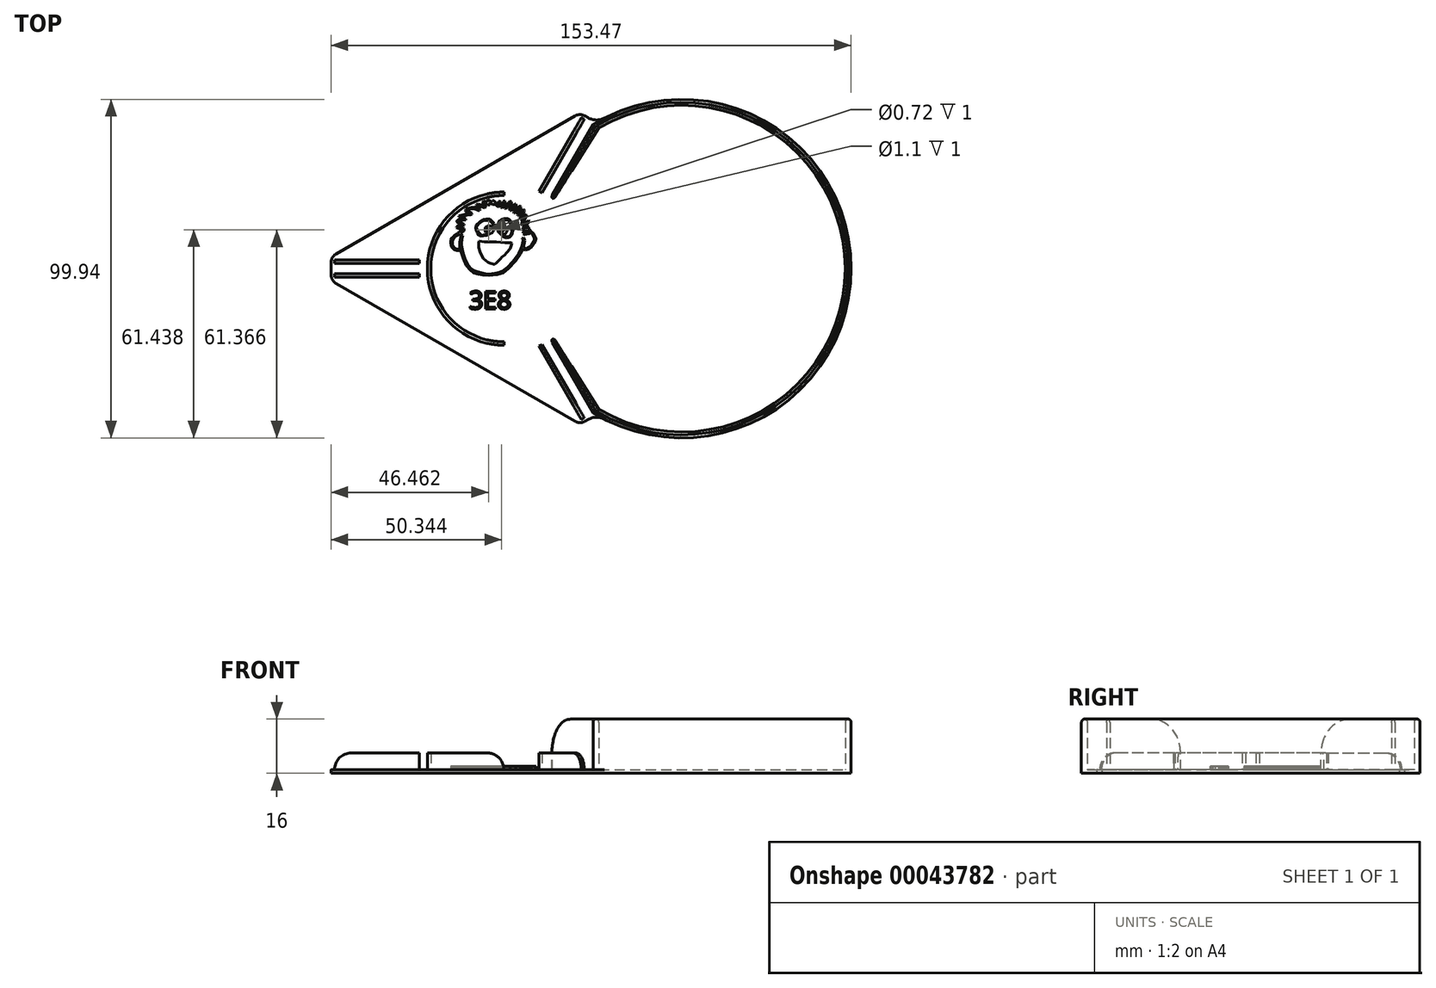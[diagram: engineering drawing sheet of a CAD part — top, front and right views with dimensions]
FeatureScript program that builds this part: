
annotation { "Feature Type Name" : "Feature", "Feature Type Description" : "" }
export const myFeature = defineFeature(function(context is Context, id is Id, definition is map)
    precondition{}
    {
        {
            var Q0;
            Q0=qCreatedBy(makeId("Top.planeOp"),FACE);
            var sketch = newSketch(context, id + "F0", { "sketchPlane" : qUnion([Q0])});
            skCircle(sketch, "E0", {"center": v(0, 0) * mm, "radius": 21.6 * mm, "construction": true});
            skLineSegment(sketch, "E1", {"start": v(0, 0) * mm, "end": v(-25, 0) * mm, "construction": true});
            skLineSegment(sketch, "E2", {"start": v(0, 0) * mm, "end": v(52.5, 0) * mm, "construction": true});
            skCircle(sketch, "E3", {"center": v(52.5, 0) * mm, "radius": 49.97 * mm});
            skLineSegment(sketch, "E4", {"start": v(-25, -1.5) * mm, "end": v(-25, 1.5) * mm, "construction": true});
            skLineSegment(sketch, "E5.bottom", {"start": v(-25, -1.5) * mm, "end": v(-50, -1.5) * mm, "construction": true});
            skLineSegment(sketch, "E5.top", {"start": v(-25, -2.5) * mm, "end": v(-50, -2.5) * mm, "construction": true});
            skLineSegment(sketch, "E5.left", {"start": v(-25, -1.5) * mm, "end": v(-25, -2.5) * mm, "construction": true});
            skLineSegment(sketch, "E5.right", {"start": v(-50, -1.5) * mm, "end": v(-50, -2.5) * mm, "construction": true});
            skLineSegment(sketch, "E6.MirrorCS", {"start": v(-25, 2.5) * mm, "end": v(-50, 2.5) * mm, "construction": true});
            skLineSegment(sketch, "E7.MirrorCS", {"start": v(-25, 1.5) * mm, "end": v(-50, 1.5) * mm, "construction": true});
            skLineSegment(sketch, "E8.MirrorCS", {"start": v(-25, 1.5) * mm, "end": v(-25, 2.5) * mm, "construction": true});
            skLineSegment(sketch, "E9.MirrorCS", {"start": v(-50, 1.5) * mm, "end": v(-50, 2.5) * mm, "construction": true});
            skLineSegment(sketch, "E10.1.0", {"start": v(11.2, -22.4) * mm, "end": v(23.7, -44.05) * mm, "construction": true});
            skLineSegment(sketch, "E10.1.1", {"start": v(14.67, -20.4) * mm, "end": v(27.17, -42.05) * mm, "construction": true});
            skLineSegment(sketch, "E10.1.2", {"start": v(10.33, -22.9) * mm, "end": v(22.83, -44.55) * mm, "construction": true});
            skLineSegment(sketch, "E10.1.3", {"start": v(13.8, -20.9) * mm, "end": v(26.3, -42.55) * mm, "construction": true});
            skLineSegment(sketch, "E10.1.4", {"start": v(13.8, -20.9) * mm, "end": v(14.67, -20.4) * mm, "construction": true});
            skLineSegment(sketch, "E10.1.5", {"start": v(26.3, -42.55) * mm, "end": v(27.17, -42.05) * mm, "construction": true});
            skLineSegment(sketch, "E10.1.6", {"start": v(11.2, -22.4) * mm, "end": v(10.33, -22.9) * mm, "construction": true});
            skLineSegment(sketch, "E10.1.7", {"start": v(23.7, -44.05) * mm, "end": v(22.83, -44.55) * mm, "construction": true});
            skLineSegment(sketch, "E10.2.0", {"start": v(13.8, 20.9) * mm, "end": v(26.3, 42.55) * mm, "construction": true});
            skLineSegment(sketch, "E10.2.1", {"start": v(10.33, 22.9) * mm, "end": v(22.83, 44.55) * mm, "construction": true});
            skLineSegment(sketch, "E10.2.2", {"start": v(14.67, 20.4) * mm, "end": v(27.17, 42.05) * mm, "construction": true});
            skLineSegment(sketch, "E10.2.3", {"start": v(11.2, 22.4) * mm, "end": v(23.7, 44.05) * mm, "construction": true});
            skLineSegment(sketch, "E10.2.4", {"start": v(11.2, 22.4) * mm, "end": v(10.33, 22.9) * mm, "construction": true});
            skLineSegment(sketch, "E10.2.5", {"start": v(23.7, 44.05) * mm, "end": v(22.83, 44.55) * mm, "construction": true});
            skLineSegment(sketch, "E10.2.6", {"start": v(13.8, 20.9) * mm, "end": v(14.67, 20.4) * mm, "construction": true});
            skLineSegment(sketch, "E10.2.7", {"start": v(26.3, 42.55) * mm, "end": v(27.17, 42.05) * mm, "construction": true});
            skCircle(sketch, "E11", {"center": v(0, 0) * mm, "radius": 26 * mm, "construction": true});
            skLineSegment(sketch, "E12.bottom", {"start": v(-51, 3.5) * mm, "end": v(-25.76, 3.5) * mm});
            skLineSegment(sketch, "E12.top", {"start": v(-51, -3.5) * mm, "end": v(-25.76, -3.5) * mm});
            skLineSegment(sketch, "E12.left", {"start": v(-51, 3.5) * mm, "end": v(-51, -3.5) * mm});
            skLineSegment(sketch, "E12.right", {"start": v(-25.76, 3.5) * mm, "end": v(-25.76, -3.5) * mm, "construction": true});
            skLineSegment(sketch, "E13", {"start": v(-50, -2.5) * mm, "end": v(-51, -2.5) * mm, "construction": true});
            skLineSegment(sketch, "E14", {"start": v(-50, 2.5) * mm, "end": v(-50, 3.5) * mm, "construction": true});
            skLineSegment(sketch, "E15", {"start": v(-25, 0) * mm, "end": v(-51, 0) * mm, "construction": true});
            skLineSegment(sketch, "E16.1.0", {"start": v(22.47, -45.92) * mm, "end": v(9.85, -24.06) * mm});
            skLineSegment(sketch, "E16.1.1", {"start": v(22.47, -45.92) * mm, "end": v(28.53, -42.42) * mm});
            skLineSegment(sketch, "E16.1.2", {"start": v(28.53, -42.42) * mm, "end": v(15.91, -20.56) * mm});
            skLineSegment(sketch, "E16.2.0", {"start": v(28.53, 42.42) * mm, "end": v(15.91, 20.56) * mm});
            skLineSegment(sketch, "E16.2.1", {"start": v(28.53, 42.42) * mm, "end": v(22.47, 45.92) * mm});
            skLineSegment(sketch, "E16.2.2", {"start": v(22.47, 45.92) * mm, "end": v(9.85, 24.06) * mm});
            skLineSegment(sketch, "E17", {"start": v(-51, -3.5) * mm, "end": v(22.47, -45.92) * mm});
            skLineSegment(sketch, "E18.MirrorCS", {"start": v(-51, 3.5) * mm, "end": v(22.47, 45.92) * mm});
            skSolve(sketch);
        }
        {
            var Q0;
            Q0 = qSketchRegion(id + "F0", true);
            extrude(context, id + "F1", {"entities" : qUnion([Q0]), "depth" : 1 * mm});
        }
        {
            var Q0;
            Q0=makeQuery(id+"F1.opExtrude","CAP_FACE",FACE,{"disambiguationData":[OSD([sQuery(id+"F0.wireOp",EDGE,"E3"),sQuery(id+"F0.wireOp",EDGE,"E11"),sQuery(id+"F0.wireOp",EDGE,"E12.bottom"),sQuery(id+"F0.wireOp",EDGE,"E12.top"),sQuery(id+"F0.wireOp",EDGE,"E12.left"),sQuery(id+"F0.wireOp",EDGE,"E16.1.0"),sQuery(id+"F0.wireOp",EDGE,"E16.1.1"),sQuery(id+"F0.wireOp",EDGE,"E16.2.1"),sQuery(id+"F0.wireOp",EDGE,"E16.2.2")])],"isStart":false});
            var sketch = newSketch(context, id + "F2", { "sketchPlane" : qUnion([Q0])});
            skLineSegment(sketch, "E19.0", {"start": v(-25, 1.5) * mm, "end": v(-50, 1.5) * mm});
            skLineSegment(sketch, "E20.0", {"start": v(-25, 2.5) * mm, "end": v(-50, 2.5) * mm});
            skLineSegment(sketch, "E21.0", {"start": v(-50, 1.5) * mm, "end": v(-50, 2.5) * mm});
            skLineSegment(sketch, "E22.0", {"start": v(-25, 1.5) * mm, "end": v(-25, 2.5) * mm});
            skLineSegment(sketch, "E23.0", {"start": v(-25, -1.5) * mm, "end": v(-50, -1.5) * mm});
            skLineSegment(sketch, "E24.0", {"start": v(-25, -2.5) * mm, "end": v(-50, -2.5) * mm});
            skLineSegment(sketch, "E25.0", {"start": v(-50, -1.5) * mm, "end": v(-50, -2.5) * mm});
            skLineSegment(sketch, "E26.0", {"start": v(-25, -1.5) * mm, "end": v(-25, -2.5) * mm});
            skLineSegment(sketch, "E27.0", {"start": v(10.33, 22.9) * mm, "end": v(22.83, 44.55) * mm});
            skLineSegment(sketch, "E28.0", {"start": v(11.2, 22.4) * mm, "end": v(23.7, 44.05) * mm});
            skLineSegment(sketch, "E29.0", {"start": v(23.7, 44.05) * mm, "end": v(22.83, 44.55) * mm});
            skLineSegment(sketch, "E30.0", {"start": v(11.2, 22.4) * mm, "end": v(10.33, 22.9) * mm});
            skLineSegment(sketch, "E31.0", {"start": v(11.2, -22.4) * mm, "end": v(23.7, -44.05) * mm});
            skLineSegment(sketch, "E32.0", {"start": v(11.2, -22.4) * mm, "end": v(10.33, -22.9) * mm});
            skLineSegment(sketch, "E33.0", {"start": v(10.33, -22.9) * mm, "end": v(22.83, -44.55) * mm});
            skLineSegment(sketch, "E34.0", {"start": v(23.7, -44.05) * mm, "end": v(22.83, -44.55) * mm});
            skCircle(sketch, "E35.0", {"center": v(0, 0) * mm, "radius": 21.6 * mm, "construction": true});
            skArc(sketch, "E36", {"start": v(0, 21.6) * mm, "mid": v(-21.6, 0) * mm, "end": v(0, -21.6) * mm});
            skArc(sketch, "E37.0", {"start": v(0, 22.6) * mm, "mid": v(-22.6, 0) * mm, "end": v(0, -22.6) * mm});
            skLineSegment(sketch, "E38", {"start": v(0, 22.6) * mm, "end": v(0, 21.6) * mm});
            skLineSegment(sketch, "E39", {"start": v(0, -21.6) * mm, "end": v(0, -22.6) * mm});
            skSolve(sketch);
        }
        {
            var Q0;
            Q0 = qSketchRegion(id + "F2", true);
            extrude(context, id + "F3", {"entities" : qUnion([Q0]), "operationType" : NewBodyOperationType.ADD, "depth" : 5 * mm});
        }
        {
            var Q0;
            Q0=makeQuery(id+"F1.opExtrude","CAP_FACE",FACE,{"disambiguationData":[OSD([sQuery(id+"F0.wireOp",EDGE,"E3"),sQuery(id+"F0.wireOp",EDGE,"E11"),sQuery(id+"F0.wireOp",EDGE,"E12.bottom"),sQuery(id+"F0.wireOp",EDGE,"E12.top"),sQuery(id+"F0.wireOp",EDGE,"E12.left"),sQuery(id+"F0.wireOp",EDGE,"E16.1.0"),sQuery(id+"F0.wireOp",EDGE,"E16.1.1"),sQuery(id+"F0.wireOp",EDGE,"E16.2.1"),sQuery(id+"F0.wireOp",EDGE,"E16.2.2")])],"isStart":false});
            var sketch = newSketch(context, id + "F4", { "sketchPlane" : qUnion([Q0])});
            skPoint(sketch, "E40.0", {"position": v(26.3, -42.55) * mm});
            skPoint(sketch, "E41.0", {"position": v(13.8, -20.9) * mm});
            skPoint(sketch, "E42.0", {"position": v(14.67, -20.4) * mm});
            skPoint(sketch, "E43.0", {"position": v(52.5, 0) * mm});
            skPoint(sketch, "E44.0", {"position": v(26.3, 42.55) * mm});
            skArc(sketch, "E45", {"start": v(26.3, -42.55) * mm, "mid": v(102.47, 0) * mm, "end": v(26.3, 42.55) * mm});
            skLineSegment(sketch, "E46", {"start": v(26.3, -42.55) * mm, "end": v(13.8, -20.9) * mm});
            skLineSegment(sketch, "E47", {"start": v(14.67, -20.4) * mm, "end": v(13.8, -20.9) * mm});
            skLineSegment(sketch, "E48.MirrorCS", {"start": v(26.3, 42.55) * mm, "end": v(13.8, 20.9) * mm});
            skLineSegment(sketch, "E49.MirrorCS", {"start": v(14.67, 20.4) * mm, "end": v(13.8, 20.9) * mm});
            skLineSegment(sketch, "E50", {"start": v(26.3, -42.55) * mm, "end": v(28.03, -41.55) * mm, "construction": true});
            skLineSegment(sketch, "E51", {"start": v(0, 0) * mm, "end": v(52.5, 0) * mm, "construction": true});
            skLineSegment(sketch, "E52.MirrorCS", {"start": v(26.3, 42.55) * mm, "end": v(28.03, 41.55) * mm, "construction": true});
            skLineSegment(sketch, "E53", {"start": v(14.67, -20.4) * mm, "end": v(28.03, -41.55) * mm});
            skLineSegment(sketch, "E54.MirrorCS", {"start": v(14.67, 20.4) * mm, "end": v(28.03, 41.55) * mm});
            skArc(sketch, "E55", {"start": v(28.03, -41.55) * mm, "mid": v(100.72, 0) * mm, "end": v(28.03, 41.55) * mm});
            skSolve(sketch);
        }
        {
            var Q0;
            Q0 = qSketchRegion(id + "F4", true);
            extrude(context, id + "F5", {"entities" : qUnion([Q0]), "operationType" : NewBodyOperationType.ADD, "depth" : 15 * mm});
        }
        {
            var Q0;
            Q0=makeQuery(id+"F1.opExtrude","SWEPT_EDGE",EDGE,{"disambiguationData":[OSD([sQuery(id+"F0.wireOp",EDGE,"E3"),sQuery(id+"F0.wireOp",EDGE,"E16.1.1")])]});
            var Q1;
            Q1=makeQuery(id+"F1.opExtrude","SWEPT_EDGE",EDGE,{"disambiguationData":[OSD([sQuery(id+"F0.wireOp",EDGE,"E3"),sQuery(id+"F0.wireOp",EDGE,"E16.1.0")])]});
            var Q2;
            {var subQ0=sQuery(id+"F0.wireOp",EDGE,"E3");var subQ1=sQuery(id+"F0.wireOp",EDGE,"E11");Q2=makeQuery(id+"F1.opExtrude","SWEPT_EDGE",EDGE,{"disambiguationData":[OSD([subQ0,subQ1]),TDD([makeQuery(id+"F0.imprint","INTERSECT",VERTEX,{"disambiguationData":[OD(1.0)],"derivedFrom":[subQ0,subQ1]})])]});}
            var Q3;
            Q3=makeQuery(id+"F1.opExtrude","SWEPT_EDGE",EDGE,{"disambiguationData":[OSD([sQuery(id+"F0.wireOp",EDGE,"E11"),sQuery(id+"F0.wireOp",EDGE,"E12.top")])]});
            var Q4;
            Q4=makeQuery(id+"F1.opExtrude","SWEPT_EDGE",EDGE,{"disambiguationData":[OSD([sQuery(id+"F0.wireOp",EDGE,"E11"),sQuery(id+"F0.wireOp",EDGE,"E12.bottom")])]});
            var Q5;
            {var subQ0=sQuery(id+"F0.wireOp",EDGE,"E3");var subQ1=sQuery(id+"F0.wireOp",EDGE,"E11");Q5=makeQuery(id+"F1.opExtrude","SWEPT_EDGE",EDGE,{"disambiguationData":[OSD([subQ0,subQ1]),TDD([makeQuery(id+"F0.imprint","INTERSECT",VERTEX,{"disambiguationData":[OD(0.0)],"derivedFrom":[subQ0,subQ1]})])]});}
            var Q6;
            Q6=makeQuery(id+"F3.opExtrude","CAP_EDGE",EDGE,{"disambiguationData":[OSD([sQuery(id+"F2.wireOp",EDGE,"E21.0")])],"isStart":false});
            var Q7;
            Q7=makeQuery(id+"F3.opExtrude","CAP_EDGE",EDGE,{"disambiguationData":[OSD([sQuery(id+"F2.wireOp",EDGE,"E25.0")])],"isStart":false});
            var Q8;
            Q8=makeQuery(id+"F3.opExtrude","CAP_EDGE",EDGE,{"disambiguationData":[OSD([sQuery(id+"F2.wireOp",EDGE,"E29.0")])],"isStart":false});
            var Q9;
            Q9=makeQuery(id+"F1.opExtrude","SWEPT_EDGE",EDGE,{"disambiguationData":[OSD([sQuery(id+"F0.wireOp",EDGE,"E3"),sQuery(id+"F0.wireOp",EDGE,"E16.2.2")])]});
            var Q10;
            Q10=makeQuery(id+"F1.opExtrude","SWEPT_EDGE",EDGE,{"disambiguationData":[OSD([sQuery(id+"F0.wireOp",EDGE,"E3"),sQuery(id+"F0.wireOp",EDGE,"E16.2.1")])]});
            var Q11;
            Q11=makeQuery(id+"F3.opExtrude","CAP_EDGE",EDGE,{"disambiguationData":[OSD([sQuery(id+"F2.wireOp",EDGE,"E39")])],"isStart":false});
            var Q12;
            Q12=makeQuery(id+"F3.opExtrude","CAP_EDGE",EDGE,{"disambiguationData":[OSD([sQuery(id+"F2.wireOp",EDGE,"E38")])],"isStart":false});
            var Q13;
            Q13=makeQuery(id+"F3.opExtrude","CAP_EDGE",EDGE,{"disambiguationData":[OSD([sQuery(id+"F2.wireOp",EDGE,"E34.0")])],"isStart":false});
            var Q14;
            Q14=makeQuery(id+"F5.opExtrude","CAP_EDGE",EDGE,{"disambiguationData":[OSD([sQuery(id+"F4.wireOp",EDGE,"65ccb3fb-5271-4e9b-97fb-ec905da2a688")])],"isStart":true});
            var Q15;
            Q15=makeQuery(id+"F5.opExtrude","CAP_EDGE",EDGE,{"disambiguationData":[OSD([sQuery(id+"F4.wireOp",EDGE,"E55")])],"isStart":true});
            fillet(context, id + "F6", {"entities" : qUnion([Q0, Q1, Q2, Q3, Q4, Q5, Q6, Q7, Q8, Q9, Q10, Q11, Q12, Q13, Q14, Q15]), "radius" : 5 * mm, "tangentPropagation" : true, "allowEdgeOverflow" : false});
        }
        {
            var Q0;
            Q0=makeQuery(id+"F5.opExtrude","CAP_EDGE",EDGE,{"disambiguationData":[OSD([sQuery(id+"F4.wireOp",EDGE,"E49.MirrorCS")])],"isStart":false});
            var Q1;
            Q1=makeQuery(id+"F5.opExtrude","CAP_EDGE",EDGE,{"disambiguationData":[OSD([sQuery(id+"F4.wireOp",EDGE,"E47")])],"isStart":false});
            fillet(context, id + "F7", {"entities" : qUnion([Q0, Q1]), "radius" : 10 * mm, "tangentPropagation" : true, "allowEdgeOverflow" : false});
        }
        {
            var Q0;
            Q0=makeQuery(id+"F1.opExtrude","SWEPT_EDGE",EDGE,{"disambiguationData":[OSD([sQuery(id+"F0.wireOp",EDGE,"E12.top"),sQuery(id+"F0.wireOp",EDGE,"E12.left")])]});
            var Q1;
            Q1=makeQuery(id+"F1.opExtrude","SWEPT_EDGE",EDGE,{"disambiguationData":[OSD([sQuery(id+"F0.wireOp",EDGE,"E12.bottom"),sQuery(id+"F0.wireOp",EDGE,"E12.left")])]});
            var Q2;
            Q2=makeQuery(id+"F1.opExtrude","SWEPT_EDGE",EDGE,{"disambiguationData":[OSD([sQuery(id+"F0.wireOp",EDGE,"E16.2.1"),sQuery(id+"F0.wireOp",EDGE,"E16.2.2")])]});
            var Q3;
            Q3=makeQuery(id+"F1.opExtrude","SWEPT_EDGE",EDGE,{"disambiguationData":[OSD([sQuery(id+"F0.wireOp",EDGE,"E16.1.0"),sQuery(id+"F0.wireOp",EDGE,"E16.1.1")])]});
            fillet(context, id + "F8", {"entities" : qUnion([Q0, Q1, Q2, Q3]), "radius" : 3 * mm, "tangentPropagation" : true, "allowEdgeOverflow" : false});
        }
        {
            var Q0;
            Q0=makeQuery(id+"F1.opExtrude","CAP_FACE",FACE,{"disambiguationData":[OSD([sQuery(id+"F0.wireOp",EDGE,"E3"),sQuery(id+"F0.wireOp",EDGE,"E12.left"),sQuery(id+"F0.wireOp",EDGE,"E16.1.1"),sQuery(id+"F0.wireOp",EDGE,"E16.2.1"),sQuery(id+"F0.wireOp",EDGE,"E17"),sQuery(id+"F0.wireOp",EDGE,"E18.MirrorCS")])],"isStart":false});
            var sketch = newSketch(context, id + "F9", { "sketchPlane" : qUnion([Q0])});
            skLineSegment(sketch, "E56", {"start": v(-12.4, 11.44) * mm, "end": v(-13.55, 10.6) * mm});
            skLineSegment(sketch, "E57", {"start": v(-13.55, 10.6) * mm, "end": v(-13.64, 10.33) * mm});
            skLineSegment(sketch, "E58", {"start": v(-13.64, 10.33) * mm, "end": v(-14.66, 9.68) * mm});
            skLineSegment(sketch, "E59", {"start": v(-14.66, 9.68) * mm, "end": v(-15.28, 9.1) * mm});
            skLineSegment(sketch, "E60", {"start": v(-15.28, 9.1) * mm, "end": v(-15.71, 8.44) * mm});
            skLineSegment(sketch, "E61", {"start": v(-15.71, 8.44) * mm, "end": v(-15.71, 7.6) * mm});
            skLineSegment(sketch, "E62", {"start": v(-15.71, 7.6) * mm, "end": v(-15.4, 6.34) * mm});
            skLineSegment(sketch, "E63", {"start": v(-15.4, 6.34) * mm, "end": v(-14.72, 5.63) * mm});
            skLineSegment(sketch, "E64", {"start": v(-14.72, 5.63) * mm, "end": v(-13.9, 5.36) * mm});
            skLineSegment(sketch, "E65", {"start": v(-13.9, 5.36) * mm, "end": v(-13.06, 5.36) * mm});
            skLineSegment(sketch, "E66", {"start": v(-13.06, 5.36) * mm, "end": v(-12.78, 5.36) * mm});
            skLineSegment(sketch, "E67", {"start": v(-12.78, 5.36) * mm, "end": v(-12, 3) * mm});
            skLineSegment(sketch, "E68", {"start": v(-12, 3) * mm, "end": v(-11.08, 0.91) * mm});
            skLineSegment(sketch, "E69", {"start": v(-11.08, 0.91) * mm, "end": v(-9.85, -0.5) * mm});
            skLineSegment(sketch, "E70", {"start": v(-9.85, -0.5) * mm, "end": v(-8.92, -1.22) * mm});
            skLineSegment(sketch, "E71", {"start": v(-8.92, -1.22) * mm, "end": v(-7.53, -1.62) * mm});
            skLineSegment(sketch, "E72", {"start": v(-7.53, -1.62) * mm, "end": v(-6.2, -1.89) * mm});
            skLineSegment(sketch, "E73", {"start": v(-6.2, -1.89) * mm, "end": v(-4.33, -2.05) * mm});
            skLineSegment(sketch, "E74", {"start": v(-4.33, -2.05) * mm, "end": v(-1.95, -1.82) * mm});
            skLineSegment(sketch, "E75", {"start": v(-1.95, -1.82) * mm, "end": v(-0.26, -1.25) * mm});
            skLineSegment(sketch, "E76", {"start": v(-0.26, -1.25) * mm, "end": v(1.32, 0) * mm});
            skLineSegment(sketch, "E77", {"start": v(1.32, 0) * mm, "end": v(3.53, 2.33) * mm});
            skLineSegment(sketch, "E78", {"start": v(3.53, 2.33) * mm, "end": v(4.84, 4.33) * mm});
            skLineSegment(sketch, "E79", {"start": v(4.84, 4.33) * mm, "end": v(5.47, 5.62) * mm});
            skLineSegment(sketch, "E80", {"start": v(5.47, 5.62) * mm, "end": v(5.66, 6.04) * mm});
            skLineSegment(sketch, "E81", {"start": v(5.66, 6.04) * mm, "end": v(5.98, 5.66) * mm});
            skLineSegment(sketch, "E82", {"start": v(5.98, 5.66) * mm, "end": v(6.42, 5.47) * mm});
            skLineSegment(sketch, "E83", {"start": v(6.42, 5.47) * mm, "end": v(7.29, 5.7) * mm});
            skLineSegment(sketch, "E84", {"start": v(7.29, 5.7) * mm, "end": v(8.1, 6.3) * mm});
            skLineSegment(sketch, "E85", {"start": v(8.1, 6.3) * mm, "end": v(9.35, 8.04) * mm});
            skLineSegment(sketch, "E86", {"start": v(9.35, 8.04) * mm, "end": v(9.5, 8.9) * mm});
            skLineSegment(sketch, "E87", {"start": v(9.5, 8.9) * mm, "end": v(8.74, 10.38) * mm});
            skLineSegment(sketch, "E88", {"start": v(8.74, 10.38) * mm, "end": v(8.1, 10.97) * mm});
            skLineSegment(sketch, "E89", {"start": v(8.1, 10.97) * mm, "end": v(7.64, 11.39) * mm});
            skLineSegment(sketch, "E90", {"start": v(7.64, 11.39) * mm, "end": v(7.17, 11.58) * mm});
            skLineSegment(sketch, "E91", {"start": v(7.17, 11.58) * mm, "end": v(7.03, 11.58) * mm});
            skLineSegment(sketch, "E92", {"start": v(7.03, 11.58) * mm, "end": v(7.38, 12.35) * mm});
            skLineSegment(sketch, "E93", {"start": v(7.38, 12.35) * mm, "end": v(7.27, 12.4) * mm});
            skLineSegment(sketch, "E94", {"start": v(7.27, 12.4) * mm, "end": v(6.45, 11.97) * mm});
            skLineSegment(sketch, "E95", {"start": v(6.45, 11.97) * mm, "end": v(6.24, 11.79) * mm});
            skLineSegment(sketch, "E96", {"start": v(6.24, 11.79) * mm, "end": v(6, 11.79) * mm});
            skLineSegment(sketch, "E97", {"start": v(6, 11.79) * mm, "end": v(6.15, 12.21) * mm});
            skLineSegment(sketch, "E98", {"start": v(6.15, 12.21) * mm, "end": v(6.8, 13) * mm});
            skLineSegment(sketch, "E99", {"start": v(6.8, 13) * mm, "end": v(7.54, 14) * mm});
            skLineSegment(sketch, "E100", {"start": v(7.54, 14) * mm, "end": v(7.25, 14.22) * mm});
            skLineSegment(sketch, "E101", {"start": v(7.25, 14.22) * mm, "end": v(5.73, 13.28) * mm});
            skLineSegment(sketch, "E102", {"start": v(5.73, 13.28) * mm, "end": v(5.6, 13.34) * mm});
            skLineSegment(sketch, "E103", {"start": v(5.6, 13.34) * mm, "end": v(5.65, 13.66) * mm});
            skLineSegment(sketch, "E104", {"start": v(5.65, 13.66) * mm, "end": v(6.71, 15.5) * mm});
            skLineSegment(sketch, "E105", {"start": v(6.71, 15.5) * mm, "end": v(6.71, 15.8) * mm});
            skLineSegment(sketch, "E106", {"start": v(6.71, 15.8) * mm, "end": v(6.57, 15.92) * mm});
            skLineSegment(sketch, "E107", {"start": v(6.57, 15.92) * mm, "end": v(6.34, 15.87) * mm});
            skLineSegment(sketch, "E108", {"start": v(6.34, 15.87) * mm, "end": v(5.32, 14.9) * mm});
            skLineSegment(sketch, "E109", {"start": v(5.32, 14.9) * mm, "end": v(5.22, 14.9) * mm});
            skLineSegment(sketch, "E110", {"start": v(5.22, 14.9) * mm, "end": v(5.22, 15.07) * mm});
            skLineSegment(sketch, "E111", {"start": v(5.22, 15.07) * mm, "end": v(6.01, 17.08) * mm});
            skLineSegment(sketch, "E112", {"start": v(6.01, 17.08) * mm, "end": v(5.96, 17.43) * mm});
            skLineSegment(sketch, "E113", {"start": v(5.96, 17.43) * mm, "end": v(5.77, 17.55) * mm});
            skLineSegment(sketch, "E114", {"start": v(5.77, 17.55) * mm, "end": v(5.27, 17.17) * mm});
            skLineSegment(sketch, "E115", {"start": v(5.27, 17.17) * mm, "end": v(4.53, 16.3) * mm});
            skLineSegment(sketch, "E116", {"start": v(4.53, 16.3) * mm, "end": v(4.43, 16.3) * mm});
            skLineSegment(sketch, "E117", {"start": v(4.43, 16.3) * mm, "end": v(5.01, 18.3) * mm});
            skLineSegment(sketch, "E118", {"start": v(5.01, 18.3) * mm, "end": v(4.93, 18.46) * mm});
            skLineSegment(sketch, "E119", {"start": v(4.93, 18.46) * mm, "end": v(4.73, 18.46) * mm});
            skLineSegment(sketch, "E120", {"start": v(4.73, 18.46) * mm, "end": v(4.5, 18.3) * mm});
            skLineSegment(sketch, "E121", {"start": v(4.5, 18.3) * mm, "end": v(3.53, 17.02) * mm});
            skLineSegment(sketch, "E122", {"start": v(3.53, 17.02) * mm, "end": v(3.43, 17.02) * mm});
            skLineSegment(sketch, "E123", {"start": v(3.43, 17.02) * mm, "end": v(3.66, 18.74) * mm});
            skLineSegment(sketch, "E124", {"start": v(3.66, 18.74) * mm, "end": v(3.49, 19.08) * mm});
            skLineSegment(sketch, "E125", {"start": v(3.49, 19.08) * mm, "end": v(3.24, 19.08) * mm});
            skLineSegment(sketch, "E126", {"start": v(3.24, 19.08) * mm, "end": v(2.24, 17.78) * mm});
            skLineSegment(sketch, "E127", {"start": v(2.24, 17.78) * mm, "end": v(2.11, 17.78) * mm});
            skLineSegment(sketch, "E128", {"start": v(2.11, 17.78) * mm, "end": v(2.16, 18.71) * mm});
            skLineSegment(sketch, "E129", {"start": v(2.16, 18.71) * mm, "end": v(2.16, 19.7) * mm});
            skLineSegment(sketch, "E130", {"start": v(2.16, 19.7) * mm, "end": v(1.97, 19.86) * mm});
            skLineSegment(sketch, "E131", {"start": v(1.97, 19.86) * mm, "end": v(1.7, 19.86) * mm});
            skLineSegment(sketch, "E132", {"start": v(1.7, 19.86) * mm, "end": v(1.46, 19.62) * mm});
            skLineSegment(sketch, "E133", {"start": v(1.46, 19.62) * mm, "end": v(0.7, 18.18) * mm});
            skLineSegment(sketch, "E134", {"start": v(0.7, 18.18) * mm, "end": v(0.6, 18.23) * mm});
            skLineSegment(sketch, "E135", {"start": v(0.6, 18.23) * mm, "end": v(0.26, 19.9) * mm});
            skLineSegment(sketch, "E136", {"start": v(0.26, 19.9) * mm, "end": v(0.05, 20) * mm});
            skLineSegment(sketch, "E137", {"start": v(0.05, 20) * mm, "end": v(-0.22, 19.82) * mm});
            skLineSegment(sketch, "E138", {"start": v(-0.22, 19.82) * mm, "end": v(-0.55, 18.6) * mm});
            skLineSegment(sketch, "E139", {"start": v(-0.55, 18.6) * mm, "end": v(-0.99, 19.7) * mm});
            skLineSegment(sketch, "E140", {"start": v(-0.99, 19.7) * mm, "end": v(-1.22, 19.88) * mm});
            skLineSegment(sketch, "E141", {"start": v(-1.22, 19.88) * mm, "end": v(-1.45, 19.88) * mm});
            skLineSegment(sketch, "E142", {"start": v(-1.45, 19.88) * mm, "end": v(-1.64, 19.8) * mm});
            skLineSegment(sketch, "E143", {"start": v(-1.64, 19.8) * mm, "end": v(-1.84, 18.84) * mm});
            skLineSegment(sketch, "E144", {"start": v(-1.84, 18.84) * mm, "end": v(-2.95, 20.04) * mm});
            skLineSegment(sketch, "E145", {"start": v(-2.95, 20.04) * mm, "end": v(-3.42, 20.04) * mm});
            skLineSegment(sketch, "E146", {"start": v(-3.42, 20.04) * mm, "end": v(-3.57, 19.85) * mm});
            skLineSegment(sketch, "E147", {"start": v(-3.57, 19.85) * mm, "end": v(-3.57, 19.77) * mm});
            skLineSegment(sketch, "E148", {"start": v(-3.57, 19.77) * mm, "end": v(-4.76, 20.37) * mm});
            skLineSegment(sketch, "E149", {"start": v(-4.76, 20.37) * mm, "end": v(-5.05, 20.27) * mm});
            skLineSegment(sketch, "E150", {"start": v(-5.05, 20.27) * mm, "end": v(-5.05, 20.05) * mm});
            skLineSegment(sketch, "E151", {"start": v(-5.05, 20.05) * mm, "end": v(-4.9, 19.6) * mm});
            skLineSegment(sketch, "E152", {"start": v(-4.9, 19.6) * mm, "end": v(-6.03, 19.94) * mm});
            skLineSegment(sketch, "E153", {"start": v(-6.03, 19.94) * mm, "end": v(-6.23, 19.83) * mm});
            skLineSegment(sketch, "E154", {"start": v(-6.23, 19.83) * mm, "end": v(-6.23, 19.5) * mm});
            skLineSegment(sketch, "E155", {"start": v(-6.23, 19.5) * mm, "end": v(-5.87, 18.53) * mm});
            skLineSegment(sketch, "E156", {"start": v(-5.87, 18.53) * mm, "end": v(-6.67, 18.8) * mm});
            skLineSegment(sketch, "E157", {"start": v(-6.67, 18.8) * mm, "end": v(-7.53, 19.1) * mm});
            skLineSegment(sketch, "E158", {"start": v(-7.53, 19.1) * mm, "end": v(-8.1, 19) * mm});
            skLineSegment(sketch, "E159", {"start": v(-8.1, 19) * mm, "end": v(-8.27, 18.7) * mm});
            skLineSegment(sketch, "E160", {"start": v(-8.27, 18.7) * mm, "end": v(-7.83, 17.8) * mm});
            skLineSegment(sketch, "E161", {"start": v(-7.83, 17.8) * mm, "end": v(-8.46, 18.03) * mm});
            skLineSegment(sketch, "E162", {"start": v(-8.46, 18.03) * mm, "end": v(-9.58, 18.03) * mm});
            skLineSegment(sketch, "E163", {"start": v(-9.58, 18.03) * mm, "end": v(-10.61, 17.86) * mm});
            skLineSegment(sketch, "E164", {"start": v(-10.61, 17.86) * mm, "end": v(-11.18, 17.6) * mm});
            skLineSegment(sketch, "E165", {"start": v(-11.18, 17.6) * mm, "end": v(-11.4, 17.32) * mm});
            skLineSegment(sketch, "E166", {"start": v(-11.4, 17.32) * mm, "end": v(-11.23, 16.95) * mm});
            skLineSegment(sketch, "E167", {"start": v(-11.23, 16.95) * mm, "end": v(-10.59, 16.41) * mm});
            skLineSegment(sketch, "E168", {"start": v(-10.59, 16.41) * mm, "end": v(-10.46, 16.27) * mm});
            skLineSegment(sketch, "E169", {"start": v(-10.46, 16.27) * mm, "end": v(-11.04, 16.17) * mm});
            skLineSegment(sketch, "E170", {"start": v(-11.04, 16.17) * mm, "end": v(-13, 15.68) * mm});
            skLineSegment(sketch, "E171", {"start": v(-13, 15.68) * mm, "end": v(-13.22, 15.47) * mm});
            skLineSegment(sketch, "E172", {"start": v(-13.22, 15.47) * mm, "end": v(-13.22, 15.28) * mm});
            skLineSegment(sketch, "E173", {"start": v(-13.22, 15.28) * mm, "end": v(-12.42, 14.76) * mm});
            skLineSegment(sketch, "E174", {"start": v(-12.42, 14.76) * mm, "end": v(-12.42, 14.65) * mm});
            skLineSegment(sketch, "E175", {"start": v(-12.42, 14.65) * mm, "end": v(-13.52, 14.33) * mm});
            skLineSegment(sketch, "E176", {"start": v(-13.52, 14.33) * mm, "end": v(-13.9, 14.06) * mm});
            skLineSegment(sketch, "E177", {"start": v(-13.9, 14.06) * mm, "end": v(-13.9, 13.83) * mm});
            skLineSegment(sketch, "E178", {"start": v(-13.9, 13.83) * mm, "end": v(-13.66, 13.55) * mm});
            skLineSegment(sketch, "E179", {"start": v(-13.66, 13.55) * mm, "end": v(-12.7, 13.04) * mm});
            skLineSegment(sketch, "E180", {"start": v(-12.7, 13.04) * mm, "end": v(-12.66, 12.95) * mm});
            skLineSegment(sketch, "E181", {"start": v(-12.66, 12.95) * mm, "end": v(-13.28, 12.73) * mm});
            skLineSegment(sketch, "E182", {"start": v(-13.28, 12.73) * mm, "end": v(-13.94, 12.3) * mm});
            skLineSegment(sketch, "E183", {"start": v(-13.94, 12.3) * mm, "end": v(-14.03, 12.12) * mm});
            skLineSegment(sketch, "E184", {"start": v(-14.03, 12.12) * mm, "end": v(-13.65, 11.94) * mm});
            skLineSegment(sketch, "E185", {"start": v(-13.65, 11.94) * mm, "end": v(-12.85, 11.67) * mm});
            skLineSegment(sketch, "E186", {"start": v(-12.85, 11.67) * mm, "end": v(-12.45, 11.6) * mm});
            skLineSegment(sketch, "E187", {"start": v(-12.45, 11.6) * mm, "end": v(-12.34, 11.55) * mm});
            skLineSegment(sketch, "E188", {"start": v(-12.34, 11.55) * mm, "end": v(-12.4, 11.44) * mm});
            skLineSegment(sketch, "E189", {"start": v(-13.32, 10.1) * mm, "end": v(-14.5, 9.37) * mm});
            skLineSegment(sketch, "E190", {"start": v(-14.5, 9.37) * mm, "end": v(-15.18, 8.44) * mm});
            skLineSegment(sketch, "E191", {"start": v(-15.18, 8.44) * mm, "end": v(-15.18, 7) * mm});
            skLineSegment(sketch, "E192", {"start": v(-15.18, 7) * mm, "end": v(-14.71, 6.23) * mm});
            skLineSegment(sketch, "E193", {"start": v(-14.71, 6.23) * mm, "end": v(-13.85, 5.7) * mm});
            skLineSegment(sketch, "E194", {"start": v(-13.85, 5.7) * mm, "end": v(-12.82, 5.7) * mm});
            skLineSegment(sketch, "E195", {"start": v(-12.82, 5.7) * mm, "end": v(-12.97, 6.35) * mm});
            skLineSegment(sketch, "E196", {"start": v(-12.97, 6.35) * mm, "end": v(-12.97, 7.8) * mm});
            skLineSegment(sketch, "E197", {"start": v(-12.97, 7.8) * mm, "end": v(-12.8, 9) * mm});
            skLineSegment(sketch, "E198", {"start": v(-12.8, 9) * mm, "end": v(-12.63, 9.7) * mm});
            skLineSegment(sketch, "E199", {"start": v(-12.63, 9.7) * mm, "end": v(-12.87, 9.96) * mm});
            skLineSegment(sketch, "E200", {"start": v(-12.87, 9.96) * mm, "end": v(-13.32, 10.1) * mm});
            skLineSegment(sketch, "E201", {"start": v(-7.27, 8.16) * mm, "end": v(-5.75, 7.96) * mm});
            skLineSegment(sketch, "E202", {"start": v(-5.75, 7.96) * mm, "end": v(-4.18, 7.9) * mm});
            skLineSegment(sketch, "E203", {"start": v(-4.18, 7.9) * mm, "end": v(-2.24, 7.94) * mm});
            skLineSegment(sketch, "E204", {"start": v(-2.24, 7.94) * mm, "end": v(0.32, 7.66) * mm});
            skLineSegment(sketch, "E205", {"start": v(0.32, 7.66) * mm, "end": v(2.27, 7.6) * mm});
            skLineSegment(sketch, "E206", {"start": v(2.27, 7.6) * mm, "end": v(2.34, 7.47) * mm});
            skLineSegment(sketch, "E207", {"start": v(2.34, 7.47) * mm, "end": v(2.25, 6.94) * mm});
            skLineSegment(sketch, "E208", {"start": v(2.25, 6.94) * mm, "end": v(1.83, 5.89) * mm});
            skLineSegment(sketch, "E209", {"start": v(1.83, 5.89) * mm, "end": v(0.85, 4.72) * mm});
            skLineSegment(sketch, "E210", {"start": v(0.85, 4.72) * mm, "end": v(0.13, 3.95) * mm});
            skLineSegment(sketch, "E211", {"start": v(0.13, 3.95) * mm, "end": v(-0.54, 3.42) * mm});
            skLineSegment(sketch, "E212", {"start": v(-0.54, 3.42) * mm, "end": v(-0.96, 2.97) * mm});
            skLineSegment(sketch, "E213", {"start": v(-0.96, 2.97) * mm, "end": v(-1.6, 2.28) * mm});
            skLineSegment(sketch, "E214", {"start": v(-1.6, 2.28) * mm, "end": v(-2.22, 1.69) * mm});
            skLineSegment(sketch, "E215", {"start": v(-2.22, 1.69) * mm, "end": v(-2.76, 1.29) * mm});
            skLineSegment(sketch, "E216", {"start": v(-2.76, 1.29) * mm, "end": v(-2.98, 1.25) * mm});
            skLineSegment(sketch, "E217", {"start": v(-2.98, 1.25) * mm, "end": v(-3.4, 1.44) * mm});
            skLineSegment(sketch, "E218", {"start": v(-3.4, 1.44) * mm, "end": v(-3.93, 1.51) * mm});
            skLineSegment(sketch, "E219", {"start": v(-3.93, 1.51) * mm, "end": v(-4.29, 1.73) * mm});
            skLineSegment(sketch, "E220", {"start": v(-4.29, 1.73) * mm, "end": v(-4.75, 1.93) * mm});
            skLineSegment(sketch, "E221", {"start": v(-4.75, 1.93) * mm, "end": v(-5.35, 2.44) * mm});
            skLineSegment(sketch, "E222", {"start": v(-5.35, 2.44) * mm, "end": v(-5.99, 2.96) * mm});
            skLineSegment(sketch, "E223", {"start": v(-5.99, 2.96) * mm, "end": v(-6.57, 3.8) * mm});
            skLineSegment(sketch, "E224", {"start": v(-6.57, 3.8) * mm, "end": v(-7.1, 4.99) * mm});
            skLineSegment(sketch, "E225", {"start": v(-7.1, 4.99) * mm, "end": v(-7.4, 6.27) * mm});
            skLineSegment(sketch, "E226", {"start": v(-7.4, 6.27) * mm, "end": v(-7.4, 7.65) * mm});
            skLineSegment(sketch, "E227", {"start": v(-7.4, 7.65) * mm, "end": v(-7.27, 8.16) * mm});
            skLineSegment(sketch, "E228", {"start": v(-12.78, 10.4) * mm, "end": v(-12.36, 9.91) * mm});
            skLineSegment(sketch, "E229", {"start": v(-12.36, 9.91) * mm, "end": v(-12.18, 9.75) * mm});
            skLineSegment(sketch, "E230", {"start": v(-12.18, 9.75) * mm, "end": v(-12.27, 9.4) * mm});
            skLineSegment(sketch, "E231", {"start": v(-12.27, 9.4) * mm, "end": v(-12.41, 8.55) * mm});
            skLineSegment(sketch, "E232", {"start": v(-12.41, 8.55) * mm, "end": v(-12.52, 7.85) * mm});
            skLineSegment(sketch, "E233", {"start": v(-12.52, 7.85) * mm, "end": v(-12.52, 6.82) * mm});
            skLineSegment(sketch, "E234", {"start": v(-12.52, 6.82) * mm, "end": v(-12.32, 5.61) * mm});
            skLineSegment(sketch, "E235", {"start": v(-12.32, 5.61) * mm, "end": v(-11.88, 4.12) * mm});
            skLineSegment(sketch, "E236", {"start": v(-11.88, 4.12) * mm, "end": v(-11.31, 2.54) * mm});
            skLineSegment(sketch, "E237", {"start": v(-11.31, 2.54) * mm, "end": v(-10.48, 0.94) * mm});
            skLineSegment(sketch, "E238", {"start": v(-10.48, 0.94) * mm, "end": v(-9.55, -0.1) * mm});
            skLineSegment(sketch, "E239", {"start": v(-9.55, -0.1) * mm, "end": v(-8.74, -0.67) * mm});
            skLineSegment(sketch, "E240", {"start": v(-8.74, -0.67) * mm, "end": v(-7.07, -1.15) * mm});
            skLineSegment(sketch, "E241", {"start": v(-7.07, -1.15) * mm, "end": v(-5.6, -1.53) * mm});
            skLineSegment(sketch, "E242", {"start": v(-5.6, -1.53) * mm, "end": v(-4.49, -1.59) * mm});
            skLineSegment(sketch, "E243", {"start": v(-4.49, -1.59) * mm, "end": v(-3.66, -1.53) * mm});
            skLineSegment(sketch, "E244", {"start": v(-3.66, -1.53) * mm, "end": v(-2.58, -1.4) * mm});
            skLineSegment(sketch, "E245", {"start": v(-2.58, -1.4) * mm, "end": v(-1.5, -1.12) * mm});
            skLineSegment(sketch, "E246", {"start": v(-1.5, -1.12) * mm, "end": v(-0.43, -0.75) * mm});
            skLineSegment(sketch, "E247", {"start": v(-0.43, -0.75) * mm, "end": v(1.04, 0.37) * mm});
            skLineSegment(sketch, "E248", {"start": v(1.04, 0.37) * mm, "end": v(2.65, 2.05) * mm});
            skLineSegment(sketch, "E249", {"start": v(2.65, 2.05) * mm, "end": v(3.53, 3.17) * mm});
            skLineSegment(sketch, "E250", {"start": v(3.53, 3.17) * mm, "end": v(4.42, 4.46) * mm});
            skLineSegment(sketch, "E251", {"start": v(4.42, 4.46) * mm, "end": v(4.97, 5.88) * mm});
            skLineSegment(sketch, "E252", {"start": v(4.97, 5.88) * mm, "end": v(5.4, 6.92) * mm});
            skLineSegment(sketch, "E253", {"start": v(5.4, 6.92) * mm, "end": v(5.64, 8.1) * mm});
            skLineSegment(sketch, "E254", {"start": v(5.64, 8.1) * mm, "end": v(5.64, 8.76) * mm});
            skLineSegment(sketch, "E255", {"start": v(5.64, 8.76) * mm, "end": v(5.53, 8.76) * mm});
            skLineSegment(sketch, "E256", {"start": v(5.53, 8.76) * mm, "end": v(5.4, 8.78) * mm});
            skLineSegment(sketch, "E257", {"start": v(5.4, 8.78) * mm, "end": v(5.4, 8.9) * mm});
            skLineSegment(sketch, "E258", {"start": v(5.4, 8.9) * mm, "end": v(5.59, 9.08) * mm});
            skLineSegment(sketch, "E259", {"start": v(5.59, 9.08) * mm, "end": v(5.74, 9.1) * mm});
            skLineSegment(sketch, "E260", {"start": v(5.74, 9.1) * mm, "end": v(5.9, 8.97) * mm});
            skLineSegment(sketch, "E261", {"start": v(5.9, 8.97) * mm, "end": v(6.07, 8.7) * mm});
            skLineSegment(sketch, "E262", {"start": v(6.07, 8.7) * mm, "end": v(6.14, 8.24) * mm});
            skLineSegment(sketch, "E263", {"start": v(6.14, 8.24) * mm, "end": v(6.05, 7.6) * mm});
            skLineSegment(sketch, "E264", {"start": v(6.05, 7.6) * mm, "end": v(5.9, 7) * mm});
            skLineSegment(sketch, "E265", {"start": v(5.9, 7) * mm, "end": v(5.82, 6.57) * mm});
            skLineSegment(sketch, "E266", {"start": v(5.82, 6.57) * mm, "end": v(5.95, 6.19) * mm});
            skLineSegment(sketch, "E267", {"start": v(5.95, 6.19) * mm, "end": v(6.27, 6) * mm});
            skLineSegment(sketch, "E268", {"start": v(6.27, 6) * mm, "end": v(6.62, 5.88) * mm});
            skLineSegment(sketch, "E269", {"start": v(6.62, 5.88) * mm, "end": v(7.3, 6.19) * mm});
            skLineSegment(sketch, "E270", {"start": v(7.3, 6.19) * mm, "end": v(8.12, 6.94) * mm});
            skLineSegment(sketch, "E271", {"start": v(8.12, 6.94) * mm, "end": v(8.8, 8.01) * mm});
            skLineSegment(sketch, "E272", {"start": v(8.8, 8.01) * mm, "end": v(8.96, 8.52) * mm});
            skLineSegment(sketch, "E273", {"start": v(8.96, 8.52) * mm, "end": v(8.96, 9.17) * mm});
            skLineSegment(sketch, "E274", {"start": v(8.96, 9.17) * mm, "end": v(8.35, 10.25) * mm});
            skLineSegment(sketch, "E275", {"start": v(8.35, 10.25) * mm, "end": v(8.08, 10.5) * mm});
            skLineSegment(sketch, "E276", {"start": v(8.08, 10.5) * mm, "end": v(7.47, 10.34) * mm});
            skLineSegment(sketch, "E277", {"start": v(7.47, 10.34) * mm, "end": v(6.65, 10.14) * mm});
            skLineSegment(sketch, "E278", {"start": v(6.65, 10.14) * mm, "end": v(5.99, 10.01) * mm});
            skLineSegment(sketch, "E279", {"start": v(5.99, 10.01) * mm, "end": v(5.84, 10) * mm});
            skLineSegment(sketch, "E280", {"start": v(5.84, 10) * mm, "end": v(5.83, 10.22) * mm});
            skLineSegment(sketch, "E281", {"start": v(5.83, 10.22) * mm, "end": v(6, 10.37) * mm});
            skLineSegment(sketch, "E282", {"start": v(6, 10.37) * mm, "end": v(5.86, 10.54) * mm});
            skLineSegment(sketch, "E283", {"start": v(5.86, 10.54) * mm, "end": v(5.68, 10.6) * mm});
            skLineSegment(sketch, "E284", {"start": v(5.68, 10.6) * mm, "end": v(5.68, 10.8) * mm});
            skLineSegment(sketch, "E285", {"start": v(5.68, 10.8) * mm, "end": v(5.85, 11.11) * mm});
            skLineSegment(sketch, "E286", {"start": v(5.85, 11.11) * mm, "end": v(6.15, 11.38) * mm});
            skLineSegment(sketch, "E287", {"start": v(6.15, 11.38) * mm, "end": v(5.65, 11.38) * mm});
            skLineSegment(sketch, "E288", {"start": v(5.65, 11.38) * mm, "end": v(5.5, 11.54) * mm});
            skLineSegment(sketch, "E289", {"start": v(5.5, 11.54) * mm, "end": v(5.59, 11.98) * mm});
            skLineSegment(sketch, "E290", {"start": v(5.59, 11.98) * mm, "end": v(5.99, 12.59) * mm});
            skLineSegment(sketch, "E291", {"start": v(5.99, 12.59) * mm, "end": v(6.12, 12.87) * mm});
            skLineSegment(sketch, "E292", {"start": v(6.12, 12.87) * mm, "end": v(6.05, 13) * mm});
            skLineSegment(sketch, "E293", {"start": v(6.05, 13) * mm, "end": v(5.44, 12.87) * mm});
            skLineSegment(sketch, "E294", {"start": v(5.44, 12.87) * mm, "end": v(5.23, 13.02) * mm});
            skLineSegment(sketch, "E295", {"start": v(5.23, 13.02) * mm, "end": v(5.23, 13.37) * mm});
            skLineSegment(sketch, "E296", {"start": v(5.23, 13.37) * mm, "end": v(5.49, 14.1) * mm});
            skLineSegment(sketch, "E297", {"start": v(5.49, 14.1) * mm, "end": v(6.03, 15.05) * mm});
            skLineSegment(sketch, "E298", {"start": v(6.03, 15.05) * mm, "end": v(5.14, 14.51) * mm});
            skLineSegment(sketch, "E299", {"start": v(5.14, 14.51) * mm, "end": v(4.88, 14.51) * mm});
            skLineSegment(sketch, "E300", {"start": v(4.88, 14.51) * mm, "end": v(4.74, 14.8) * mm});
            skLineSegment(sketch, "E301", {"start": v(4.74, 14.8) * mm, "end": v(5.4, 16.72) * mm});
            skLineSegment(sketch, "E302", {"start": v(5.4, 16.72) * mm, "end": v(4.27, 15.67) * mm});
            skLineSegment(sketch, "E303", {"start": v(4.27, 15.67) * mm, "end": v(4.1, 15.65) * mm});
            skLineSegment(sketch, "E304", {"start": v(4.1, 15.65) * mm, "end": v(3.97, 15.85) * mm});
            skLineSegment(sketch, "E305", {"start": v(3.97, 15.85) * mm, "end": v(4.37, 17.53) * mm});
            skLineSegment(sketch, "E306", {"start": v(4.37, 17.53) * mm, "end": v(3.15, 16.35) * mm});
            skLineSegment(sketch, "E307", {"start": v(3.15, 16.35) * mm, "end": v(2.98, 16.46) * mm});
            skLineSegment(sketch, "E308", {"start": v(2.98, 16.46) * mm, "end": v(2.87, 16.72) * mm});
            skLineSegment(sketch, "E309", {"start": v(2.87, 16.72) * mm, "end": v(3.25, 18.48) * mm});
            skLineSegment(sketch, "E310", {"start": v(3.25, 18.48) * mm, "end": v(2.11, 17.15) * mm});
            skLineSegment(sketch, "E311", {"start": v(2.11, 17.15) * mm, "end": v(1.86, 17.15) * mm});
            skLineSegment(sketch, "E312", {"start": v(1.86, 17.15) * mm, "end": v(1.7, 17.36) * mm});
            skLineSegment(sketch, "E313", {"start": v(1.7, 17.36) * mm, "end": v(1.7, 19.33) * mm});
            skLineSegment(sketch, "E314", {"start": v(1.7, 19.33) * mm, "end": v(0.9, 17.9) * mm});
            skLineSegment(sketch, "E315", {"start": v(0.9, 17.9) * mm, "end": v(0.57, 17.7) * mm});
            skLineSegment(sketch, "E316", {"start": v(0.57, 17.7) * mm, "end": v(0.38, 17.79) * mm});
            skLineSegment(sketch, "E317", {"start": v(0.38, 17.79) * mm, "end": v(0.04, 19) * mm});
            skLineSegment(sketch, "E318", {"start": v(0.04, 19) * mm, "end": v(-0.19, 18.28) * mm});
            skLineSegment(sketch, "E319", {"start": v(-0.19, 18.28) * mm, "end": v(-0.55, 17.93) * mm});
            skLineSegment(sketch, "E320", {"start": v(-0.55, 17.93) * mm, "end": v(-0.84, 18.04) * mm});
            skLineSegment(sketch, "E321", {"start": v(-0.84, 18.04) * mm, "end": v(-1.26, 19.03) * mm});
            skLineSegment(sketch, "E322", {"start": v(-1.26, 19.03) * mm, "end": v(-1.38, 18.5) * mm});
            skLineSegment(sketch, "E323", {"start": v(-1.38, 18.5) * mm, "end": v(-1.64, 18.28) * mm});
            skLineSegment(sketch, "E324", {"start": v(-1.64, 18.28) * mm, "end": v(-1.84, 18.28) * mm});
            skLineSegment(sketch, "E325", {"start": v(-1.84, 18.28) * mm, "end": v(-2.76, 19.1) * mm});
            skLineSegment(sketch, "E326", {"start": v(-2.76, 19.1) * mm, "end": v(-2.94, 18.9) * mm});
            skLineSegment(sketch, "E327", {"start": v(-2.94, 18.9) * mm, "end": v(-3.41, 18.9) * mm});
            skLineSegment(sketch, "E328", {"start": v(-3.41, 18.9) * mm, "end": v(-4.17, 19.61) * mm});
            skLineSegment(sketch, "E329", {"start": v(-4.17, 19.61) * mm, "end": v(-4.25, 19.53) * mm});
            skLineSegment(sketch, "E330", {"start": v(-4.25, 19.53) * mm, "end": v(-3.96, 19.04) * mm});
            skLineSegment(sketch, "E331", {"start": v(-3.96, 19.04) * mm, "end": v(-4.1, 18.85) * mm});
            skLineSegment(sketch, "E332", {"start": v(-4.1, 18.85) * mm, "end": v(-4.8, 18.85) * mm});
            skLineSegment(sketch, "E333", {"start": v(-4.8, 18.85) * mm, "end": v(-5.55, 19.36) * mm});
            skLineSegment(sketch, "E334", {"start": v(-5.55, 19.36) * mm, "end": v(-5.61, 19.27) * mm});
            skLineSegment(sketch, "E335", {"start": v(-5.61, 19.27) * mm, "end": v(-5.37, 18.8) * mm});
            skLineSegment(sketch, "E336", {"start": v(-5.37, 18.8) * mm, "end": v(-5.37, 18.13) * mm});
            skLineSegment(sketch, "E337", {"start": v(-5.37, 18.13) * mm, "end": v(-5.6, 17.94) * mm});
            skLineSegment(sketch, "E338", {"start": v(-5.6, 17.94) * mm, "end": v(-7.75, 18.68) * mm});
            skLineSegment(sketch, "E339", {"start": v(-7.75, 18.68) * mm, "end": v(-7, 17.5) * mm});
            skLineSegment(sketch, "E340", {"start": v(-7, 17.5) * mm, "end": v(-7.22, 17.21) * mm});
            skLineSegment(sketch, "E341", {"start": v(-7.22, 17.21) * mm, "end": v(-7.6, 17.21) * mm});
            skLineSegment(sketch, "E342", {"start": v(-7.6, 17.21) * mm, "end": v(-8.02, 17.44) * mm});
            skLineSegment(sketch, "E343", {"start": v(-8.02, 17.44) * mm, "end": v(-9, 17.61) * mm});
            skLineSegment(sketch, "E344", {"start": v(-9, 17.61) * mm, "end": v(-10.15, 17.61) * mm});
            skLineSegment(sketch, "E345", {"start": v(-10.15, 17.61) * mm, "end": v(-10.92, 17.38) * mm});
            skLineSegment(sketch, "E346", {"start": v(-10.92, 17.38) * mm, "end": v(-10.83, 17.17) * mm});
            skLineSegment(sketch, "E347", {"start": v(-10.83, 17.17) * mm, "end": v(-9.52, 16.28) * mm});
            skLineSegment(sketch, "E348", {"start": v(-9.52, 16.28) * mm, "end": v(-9.47, 16.07) * mm});
            skLineSegment(sketch, "E349", {"start": v(-9.47, 16.07) * mm, "end": v(-9.84, 15.86) * mm});
            skLineSegment(sketch, "E350", {"start": v(-9.84, 15.86) * mm, "end": v(-11.01, 15.78) * mm});
            skLineSegment(sketch, "E351", {"start": v(-11.01, 15.78) * mm, "end": v(-12.31, 15.44) * mm});
            skLineSegment(sketch, "E352", {"start": v(-12.31, 15.44) * mm, "end": v(-12.48, 15.44) * mm});
            skLineSegment(sketch, "E353", {"start": v(-12.48, 15.44) * mm, "end": v(-12.48, 15.32) * mm});
            skLineSegment(sketch, "E354", {"start": v(-12.48, 15.32) * mm, "end": v(-11.18, 14.68) * mm});
            skLineSegment(sketch, "E355", {"start": v(-11.18, 14.68) * mm, "end": v(-11.18, 14.47) * mm});
            skLineSegment(sketch, "E356", {"start": v(-11.18, 14.47) * mm, "end": v(-11.28, 14.4) * mm});
            skLineSegment(sketch, "E357", {"start": v(-11.28, 14.4) * mm, "end": v(-13.28, 14.06) * mm});
            skLineSegment(sketch, "E358", {"start": v(-13.28, 14.06) * mm, "end": v(-13.25, 13.88) * mm});
            skLineSegment(sketch, "E359", {"start": v(-13.25, 13.88) * mm, "end": v(-12, 13.2) * mm});
            skLineSegment(sketch, "E360", {"start": v(-12, 13.2) * mm, "end": v(-11.79, 13.07) * mm});
            skLineSegment(sketch, "E361", {"start": v(-11.79, 13.07) * mm, "end": v(-11.75, 12.86) * mm});
            skLineSegment(sketch, "E362", {"start": v(-11.75, 12.86) * mm, "end": v(-13.3, 12.3) * mm});
            skLineSegment(sketch, "E363", {"start": v(-13.3, 12.3) * mm, "end": v(-11.81, 11.86) * mm});
            skLineSegment(sketch, "E364", {"start": v(-11.81, 11.86) * mm, "end": v(-11.81, 11.4) * mm});
            skLineSegment(sketch, "E365", {"start": v(-11.81, 11.4) * mm, "end": v(-11.92, 11.05) * mm});
            skLineSegment(sketch, "E366", {"start": v(-11.92, 11.05) * mm, "end": v(-12.78, 10.4) * mm});
            skLineSegment(sketch, "E367", {"start": v(-6.15, 14.5) * mm, "end": v(-7.1, 13.85) * mm});
            skLineSegment(sketch, "E368", {"start": v(-7.1, 13.85) * mm, "end": v(-8.17, 12.88) * mm});
            skLineSegment(sketch, "E369", {"start": v(-8.17, 12.88) * mm, "end": v(-8.38, 11.97) * mm});
            skLineSegment(sketch, "E370", {"start": v(-8.38, 11.97) * mm, "end": v(-8.25, 11.42) * mm});
            skLineSegment(sketch, "E371", {"start": v(-8.25, 11.42) * mm, "end": v(-7.83, 10.56) * mm});
            skLineSegment(sketch, "E372", {"start": v(-7.83, 10.56) * mm, "end": v(-7.4, 9.99) * mm});
            skLineSegment(sketch, "E373", {"start": v(-7.4, 9.99) * mm, "end": v(-6.92, 9.49) * mm});
            skLineSegment(sketch, "E374", {"start": v(-6.92, 9.49) * mm, "end": v(-5.11, 9.85) * mm});
            skLineSegment(sketch, "E375", {"start": v(-5.11, 9.85) * mm, "end": v(-4.18, 10.37) * mm});
            skLineSegment(sketch, "E376", {"start": v(-4.18, 10.37) * mm, "end": v(-3.54, 10.54) * mm});
            skLineSegment(sketch, "E377", {"start": v(-3.54, 10.54) * mm, "end": v(-3.1, 11.06) * mm});
            skLineSegment(sketch, "E378", {"start": v(-3.1, 11.06) * mm, "end": v(-3.02, 11.57) * mm});
            skLineSegment(sketch, "E379", {"start": v(-3.02, 11.57) * mm, "end": v(-3.08, 12.07) * mm});
            skLineSegment(sketch, "E380", {"start": v(-3.08, 12.07) * mm, "end": v(-2.92, 13.3) * mm});
            skLineSegment(sketch, "E381", {"start": v(-2.92, 13.3) * mm, "end": v(-3.08, 13.6) * mm});
            skLineSegment(sketch, "E382", {"start": v(-3.08, 13.6) * mm, "end": v(-3.69, 14.25) * mm});
            skLineSegment(sketch, "E383", {"start": v(-3.69, 14.25) * mm, "end": v(-4.16, 14.57) * mm});
            skLineSegment(sketch, "E384", {"start": v(-4.16, 14.57) * mm, "end": v(-4.73, 14.68) * mm});
            skLineSegment(sketch, "E385", {"start": v(-4.73, 14.68) * mm, "end": v(-5.33, 14.68) * mm});
            skLineSegment(sketch, "E386", {"start": v(-5.33, 14.68) * mm, "end": v(-6.15, 14.5) * mm});
            skLineSegment(sketch, "E387", {"start": v(-3.4, 12.34) * mm, "end": v(-4.05, 12.59) * mm});
            skLineSegment(sketch, "E388", {"start": v(-4.05, 12.59) * mm, "end": v(-4.89, 12.6) * mm});
            skLineSegment(sketch, "E389", {"start": v(-4.89, 12.6) * mm, "end": v(-5.36, 12.27) * mm});
            skLineSegment(sketch, "E390", {"start": v(-5.36, 12.27) * mm, "end": v(-5.59, 11.78) * mm});
            skLineSegment(sketch, "E391", {"start": v(-5.59, 11.78) * mm, "end": v(-5.58, 11.17) * mm});
            skLineSegment(sketch, "E392", {"start": v(-5.58, 11.17) * mm, "end": v(-5.37, 10.74) * mm});
            skLineSegment(sketch, "E393", {"start": v(-5.37, 10.74) * mm, "end": v(-5.09, 10.5) * mm});
            skLineSegment(sketch, "E394", {"start": v(-5.09, 10.5) * mm, "end": v(-4.93, 10.49) * mm});
            skLineSegment(sketch, "E395", {"start": v(-4.93, 10.49) * mm, "end": v(-4.86, 10.42) * mm});
            skLineSegment(sketch, "E396", {"start": v(-4.86, 10.42) * mm, "end": v(-4.9, 10.3) * mm});
            skLineSegment(sketch, "E397", {"start": v(-4.9, 10.3) * mm, "end": v(-5.13, 10.2) * mm});
            skLineSegment(sketch, "E398", {"start": v(-5.13, 10.2) * mm, "end": v(-5.56, 10.08) * mm});
            skLineSegment(sketch, "E399", {"start": v(-5.56, 10.08) * mm, "end": v(-5.98, 9.91) * mm});
            skLineSegment(sketch, "E400", {"start": v(-5.98, 9.91) * mm, "end": v(-6.35, 9.84) * mm});
            skLineSegment(sketch, "E401", {"start": v(-6.35, 9.84) * mm, "end": v(-6.65, 9.88) * mm});
            skLineSegment(sketch, "E402", {"start": v(-6.65, 9.88) * mm, "end": v(-7.57, 10.79) * mm});
            skLineSegment(sketch, "E403", {"start": v(-7.57, 10.79) * mm, "end": v(-7.92, 11.48) * mm});
            skLineSegment(sketch, "E404", {"start": v(-7.92, 11.48) * mm, "end": v(-8.06, 12.31) * mm});
            skLineSegment(sketch, "E405", {"start": v(-8.06, 12.31) * mm, "end": v(-7.45, 13.2) * mm});
            skLineSegment(sketch, "E406", {"start": v(-7.45, 13.2) * mm, "end": v(-6.44, 14) * mm});
            skLineSegment(sketch, "E407", {"start": v(-6.44, 14) * mm, "end": v(-5.77, 14.28) * mm});
            skLineSegment(sketch, "E408", {"start": v(-5.77, 14.28) * mm, "end": v(-4.82, 14.3) * mm});
            skLineSegment(sketch, "E409", {"start": v(-4.82, 14.3) * mm, "end": v(-4.1, 14.12) * mm});
            skLineSegment(sketch, "E410", {"start": v(-4.1, 14.12) * mm, "end": v(-3.66, 13.56) * mm});
            skLineSegment(sketch, "E411", {"start": v(-3.66, 13.56) * mm, "end": v(-3.26, 13.09) * mm});
            skLineSegment(sketch, "E412", {"start": v(-3.26, 13.09) * mm, "end": v(-3.27, 12.72) * mm});
            skLineSegment(sketch, "E413", {"start": v(-3.27, 12.72) * mm, "end": v(-3.4, 12.34) * mm});
            skCircle(sketch, "E414", {"center": v(-4.54, 11.47) * mm, "radius": 0.36 * mm});
            skCircle(sketch, "E415", {"center": v(-0.66, 11.4) * mm, "radius": 0.55 * mm});
            skLineSegment(sketch, "E416", {"start": v(-1.38, 12.17) * mm, "end": v(-1.46, 12.93) * mm});
            skLineSegment(sketch, "E417", {"start": v(-1.46, 12.93) * mm, "end": v(-1.18, 13.71) * mm});
            skLineSegment(sketch, "E418", {"start": v(-1.18, 13.71) * mm, "end": v(-0.7, 14.2) * mm});
            skLineSegment(sketch, "E419", {"start": v(-0.7, 14.2) * mm, "end": v(-0.05, 14.4) * mm});
            skLineSegment(sketch, "E420", {"start": v(-0.05, 14.4) * mm, "end": v(0.81, 14.41) * mm});
            skLineSegment(sketch, "E421", {"start": v(0.81, 14.41) * mm, "end": v(1.18, 14.32) * mm});
            skLineSegment(sketch, "E422", {"start": v(1.18, 14.32) * mm, "end": v(1.58, 13.8) * mm});
            skLineSegment(sketch, "E423", {"start": v(1.58, 13.8) * mm, "end": v(1.96, 13.07) * mm});
            skLineSegment(sketch, "E424", {"start": v(1.96, 13.07) * mm, "end": v(2.35, 12.05) * mm});
            skLineSegment(sketch, "E425", {"start": v(2.35, 12.05) * mm, "end": v(2.4, 11.39) * mm});
            skLineSegment(sketch, "E426", {"start": v(2.4, 11.39) * mm, "end": v(2.3, 10.83) * mm});
            skLineSegment(sketch, "E427", {"start": v(2.3, 10.83) * mm, "end": v(2.06, 10.1) * mm});
            skLineSegment(sketch, "E428", {"start": v(2.06, 10.1) * mm, "end": v(1.87, 9.78) * mm});
            skLineSegment(sketch, "E429", {"start": v(1.87, 9.78) * mm, "end": v(1.4, 9.46) * mm});
            skLineSegment(sketch, "E430", {"start": v(1.4, 9.46) * mm, "end": v(0.8, 9.39) * mm});
            skLineSegment(sketch, "E431", {"start": v(0.8, 9.39) * mm, "end": v(0.15, 9.65) * mm});
            skLineSegment(sketch, "E432", {"start": v(0.15, 9.65) * mm, "end": v(-0.3, 9.94) * mm});
            skLineSegment(sketch, "E433", {"start": v(-0.3, 9.94) * mm, "end": v(-0.55, 10.22) * mm});
            skLineSegment(sketch, "E434", {"start": v(-0.55, 10.22) * mm, "end": v(0.09, 10.22) * mm});
            skLineSegment(sketch, "E435", {"start": v(0.09, 10.22) * mm, "end": v(0.5, 10.32) * mm});
            skLineSegment(sketch, "E436", {"start": v(0.5, 10.32) * mm, "end": v(0.8, 10.75) * mm});
            skLineSegment(sketch, "E437", {"start": v(0.8, 10.75) * mm, "end": v(1, 11.37) * mm});
            skLineSegment(sketch, "E438", {"start": v(1, 11.37) * mm, "end": v(0.8, 12.01) * mm});
            skLineSegment(sketch, "E439", {"start": v(0.8, 12.01) * mm, "end": v(0.28, 12.37) * mm});
            skLineSegment(sketch, "E440", {"start": v(0.28, 12.37) * mm, "end": v(-0.38, 12.37) * mm});
            skLineSegment(sketch, "E441", {"start": v(-0.38, 12.37) * mm, "end": v(-0.96, 12.29) * mm});
            skLineSegment(sketch, "E442", {"start": v(-0.96, 12.29) * mm, "end": v(-1.38, 12.17) * mm});
            skLineSegment(sketch, "E443", {"start": v(-1.66, 11.8) * mm, "end": v(-1.76, 12.23) * mm});
            skLineSegment(sketch, "E444", {"start": v(-1.76, 12.23) * mm, "end": v(-1.81, 12.78) * mm});
            skLineSegment(sketch, "E445", {"start": v(-1.81, 12.78) * mm, "end": v(-1.63, 13.48) * mm});
            skLineSegment(sketch, "E446", {"start": v(-1.63, 13.48) * mm, "end": v(-1.28, 14.06) * mm});
            skLineSegment(sketch, "E447", {"start": v(-1.28, 14.06) * mm, "end": v(-0.73, 14.5) * mm});
            skLineSegment(sketch, "E448", {"start": v(-0.73, 14.5) * mm, "end": v(-0.01, 14.7) * mm});
            skLineSegment(sketch, "E449", {"start": v(-0.01, 14.7) * mm, "end": v(0.6, 14.74) * mm});
            skLineSegment(sketch, "E450", {"start": v(0.6, 14.74) * mm, "end": v(1.08, 14.7) * mm});
            skLineSegment(sketch, "E451", {"start": v(1.08, 14.7) * mm, "end": v(1.58, 14.47) * mm});
            skLineSegment(sketch, "E452", {"start": v(1.58, 14.47) * mm, "end": v(1.95, 14.1) * mm});
            skLineSegment(sketch, "E453", {"start": v(1.95, 14.1) * mm, "end": v(2.23, 13.57) * mm});
            skLineSegment(sketch, "E454", {"start": v(2.23, 13.57) * mm, "end": v(2.64, 12.82) * mm});
            skLineSegment(sketch, "E455", {"start": v(2.64, 12.82) * mm, "end": v(2.85, 12.15) * mm});
            skLineSegment(sketch, "E456", {"start": v(2.85, 12.15) * mm, "end": v(2.79, 11.62) * mm});
            skLineSegment(sketch, "E457", {"start": v(2.79, 11.62) * mm, "end": v(2.6, 11.03) * mm});
            skLineSegment(sketch, "E458", {"start": v(2.6, 11.03) * mm, "end": v(2.47, 10.36) * mm});
            skLineSegment(sketch, "E459", {"start": v(2.47, 10.36) * mm, "end": v(2.22, 9.75) * mm});
            skLineSegment(sketch, "E460", {"start": v(2.22, 9.75) * mm, "end": v(1.66, 9.3) * mm});
            skLineSegment(sketch, "E461", {"start": v(1.66, 9.3) * mm, "end": v(1.3, 9.12) * mm});
            skLineSegment(sketch, "E462", {"start": v(1.3, 9.12) * mm, "end": v(0.74, 9.01) * mm});
            skLineSegment(sketch, "E463", {"start": v(0.74, 9.01) * mm, "end": v(0.2, 9.23) * mm});
            skLineSegment(sketch, "E464", {"start": v(0.2, 9.23) * mm, "end": v(-0.5, 9.65) * mm});
            skLineSegment(sketch, "E465", {"start": v(-0.5, 9.65) * mm, "end": v(-1.02, 10.23) * mm});
            skLineSegment(sketch, "E466", {"start": v(-1.02, 10.23) * mm, "end": v(-1.3, 10.53) * mm});
            skLineSegment(sketch, "E467", {"start": v(-1.3, 10.53) * mm, "end": v(-1.7, 10.86) * mm});
            skLineSegment(sketch, "E468", {"start": v(-1.7, 10.86) * mm, "end": v(-1.78, 11.33) * mm});
            skLineSegment(sketch, "E469", {"start": v(-1.78, 11.33) * mm, "end": v(-1.66, 11.8) * mm});
            skLineSegment(sketch, "E470", {"start": v(6.73, 11.26) * mm, "end": v(6.4, 11.06) * mm});
            skLineSegment(sketch, "E471", {"start": v(6.4, 11.06) * mm, "end": v(6.2, 10.88) * mm});
            skLineSegment(sketch, "E472", {"start": v(6.2, 10.88) * mm, "end": v(6.37, 10.75) * mm});
            skLineSegment(sketch, "E473", {"start": v(6.37, 10.75) * mm, "end": v(6.8, 10.7) * mm});
            skLineSegment(sketch, "E474", {"start": v(6.8, 10.7) * mm, "end": v(7.38, 10.8) * mm});
            skLineSegment(sketch, "E475", {"start": v(7.38, 10.8) * mm, "end": v(7.67, 10.85) * mm});
            skLineSegment(sketch, "E476", {"start": v(7.67, 10.85) * mm, "end": v(7.6, 11.02) * mm});
            skLineSegment(sketch, "E477", {"start": v(7.6, 11.02) * mm, "end": v(7.36, 11.2) * mm});
            skLineSegment(sketch, "E478", {"start": v(7.36, 11.2) * mm, "end": v(6.95, 11.3) * mm});
            skLineSegment(sketch, "E479", {"start": v(6.95, 11.3) * mm, "end": v(6.73, 11.26) * mm});
            skText(sketch, "E480", { "text": "3E8", "fontName": "OpenSans-Regular.ttf"});
            const initialGuessF9  = {"E480": [-0.0103, -0.01192, 1, 0, 0.00528]};
            skSetInitialGuess(sketch, initialGuessF9);
            skSolve(sketch);
        }
        {
            var Q0;
            Q0 = qSketchRegion(id + "F9", true);
            var Q1;
            Q1=makeQuery(id+"F9.imprint","IMPRINT",FACE,{"disambiguationData":[TD([[makeQuery(id+"F9.imprint","IMPRINT",EDGE,{"derivedFrom":sQuery(id+"F9.wireOp",EDGE,"E367")}),1.0]])]});
            var Q2;
            Q2=makeQuery(id+"F9.imprint","IMPRINT",FACE,{"disambiguationData":[TD([[makeQuery(id+"F9.imprint","IMPRINT",EDGE,{"derivedFrom":sQuery(id+"F9.wireOp",EDGE,"E201")}),-1.0]])]});
            var Q3;
            Q3=makeQuery(id+"F9.imprint","IMPRINT",FACE,{"disambiguationData":[TD([[makeQuery(id+"F9.imprint","IMPRINT",EDGE,{"derivedFrom":sQuery(id+"F9.wireOp",EDGE,"E415")}),-1.0]])]});
            extrude(context, id + "F10", {"entities" : qUnion([Q0, Q1, Q2, Q3]), "operationType" : NewBodyOperationType.ADD, "depth" : 1 * mm});
        }
        {
            var Q0;
            Q0=makeQuery(id+"F5.opExtrude","CAP_FACE",FACE,{"disambiguationData":[OSD([sQuery(id+"F4.wireOp",EDGE,"E45"),sQuery(id+"F4.wireOp",EDGE,"E46"),sQuery(id+"F4.wireOp",EDGE,"E47"),sQuery(id+"F4.wireOp",EDGE,"E48.MirrorCS"),sQuery(id+"F4.wireOp",EDGE,"E49.MirrorCS"),sQuery(id+"F4.wireOp",EDGE,"E53"),sQuery(id+"F4.wireOp",EDGE,"E54.MirrorCS"),sQuery(id+"F4.wireOp",EDGE,"E55")])],"isStart":false});
            fillet(context, id + "F11", {"entities" : qUnion([Q0]), "radius" : 1 * mm, "tangentPropagation" : true, "allowEdgeOverflow" : false});
        }
    });
